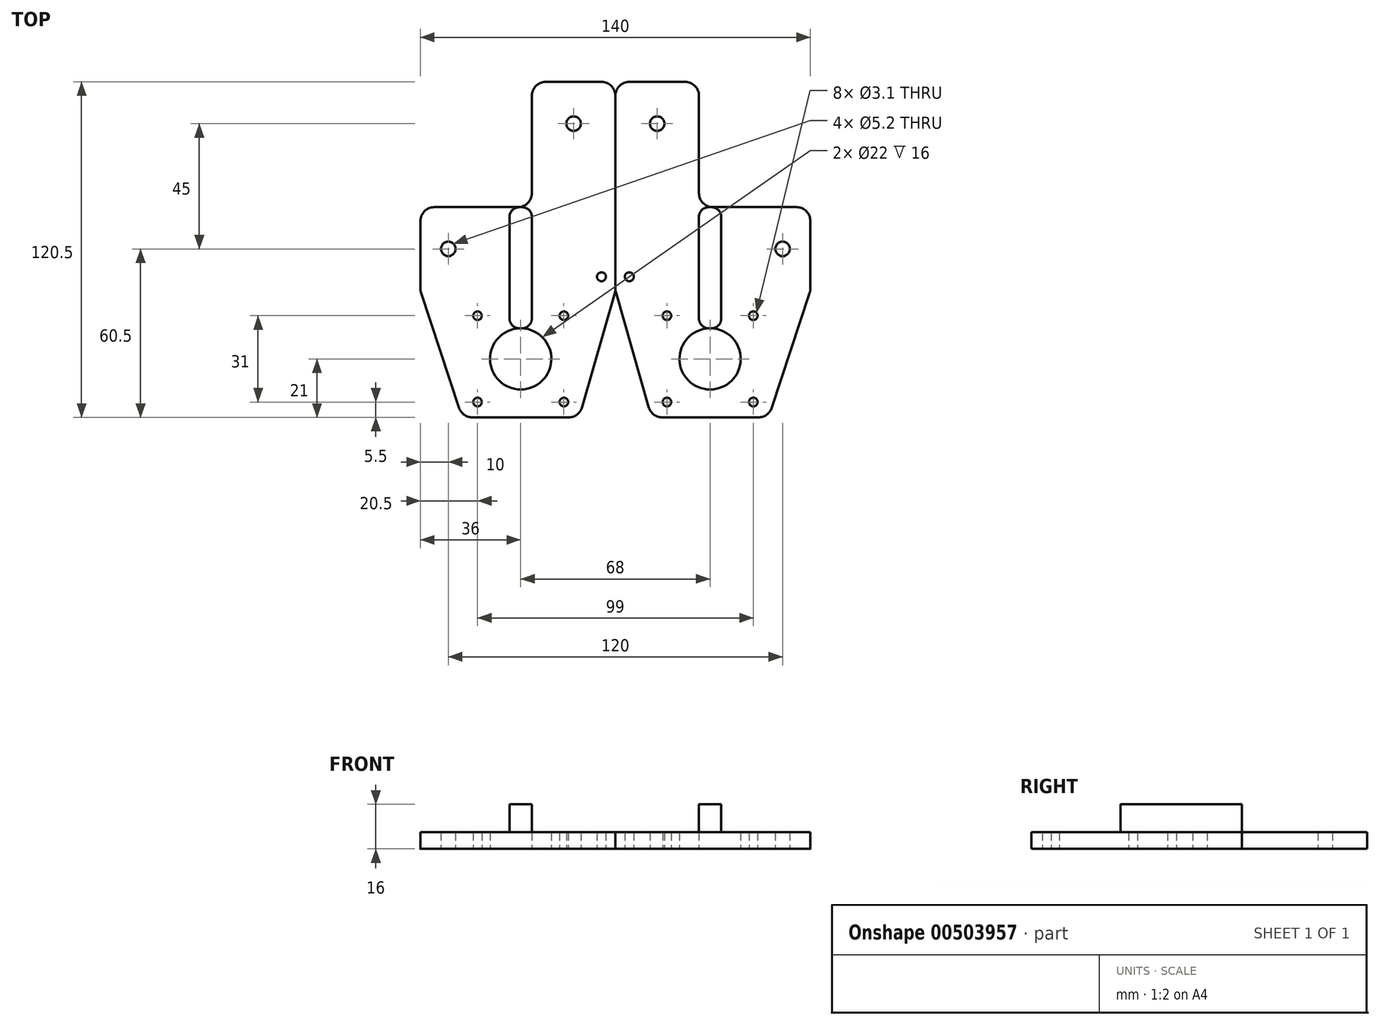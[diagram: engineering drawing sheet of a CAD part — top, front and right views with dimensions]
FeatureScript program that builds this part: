
annotation { "Feature Type Name" : "Feature", "Feature Type Description" : "" }
export const myFeature = defineFeature(function(context is Context, id is Id, definition is map)
    precondition{}
    {
        {
            var Q0;
            Q0=qCreatedBy(makeId("Top.planeOp"),FACE);
            var sketch = newSketch(context, id + "F0", { "sketchPlane" : qUnion([Q0])});
            skLineSegment(sketch, "E0.bottom", {"start": v(35, -60.25) * mm, "end": v(-35, -60.25) * mm});
            skLineSegment(sketch, "E0.left", {"start": v(35, -60.25) * mm, "end": v(35, 60.25) * mm});
            skLineSegment(sketch, "E0.right", {"start": v(-35, -60.25) * mm, "end": v(-35, 60.25) * mm});
            skPoint(sketch, "E0.middle", {"position": v(0, 0) * mm});
            skCircle(sketch, "E1", {"center": v(-1, -39.25) * mm, "radius": 11 * mm});
            skLineSegment(sketch, "E2.bottom", {"start": v(14.5, -54.75) * mm, "end": v(-16.5, -54.75) * mm, "construction": true});
            skLineSegment(sketch, "E2.top", {"start": v(14.5, -23.75) * mm, "end": v(-16.5, -23.75) * mm, "construction": true});
            skLineSegment(sketch, "E2.left", {"start": v(14.5, -54.75) * mm, "end": v(14.5, -23.75) * mm, "construction": true});
            skLineSegment(sketch, "E2.right", {"start": v(-16.5, -54.75) * mm, "end": v(-16.5, -23.75) * mm, "construction": true});
            skCircle(sketch, "E3", {"center": v(-16.5, -23.75) * mm, "radius": 1.55 * mm});
            skCircle(sketch, "E4", {"center": v(-16.5, -54.75) * mm, "radius": 1.55 * mm});
            skCircle(sketch, "E5", {"center": v(14.5, -54.75) * mm, "radius": 1.55 * mm});
            skCircle(sketch, "E6", {"center": v(14.5, -23.75) * mm, "radius": 1.55 * mm});
            skLineSegment(sketch, "E7", {"start": v(-35, 60.25) * mm, "end": v(35, 60.25) * mm});
            skLineSegment(sketch, "E8.bottom", {"start": v(35, 60.25) * mm, "end": v(-5, 60.25) * mm});
            skLineSegment(sketch, "E8.top", {"start": v(35, 15.25) * mm, "end": v(-5, 15.25) * mm});
            skLineSegment(sketch, "E8.left", {"start": v(35, 60.25) * mm, "end": v(35, 15.25) * mm});
            skLineSegment(sketch, "E8.right", {"start": v(-5, 60.25) * mm, "end": v(-5, 15.25) * mm});
            skLineSegment(sketch, "E9", {"start": v(-35, -14.75) * mm, "end": v(-22, -60.25) * mm});
            skLineSegment(sketch, "E10", {"start": v(35, -14.75) * mm, "end": v(20, -60.25) * mm});
            skLineSegment(sketch, "E11", {"start": v(-20, 60.25) * mm, "end": v(-20, 0.25) * mm, "construction": true});
            skCircle(sketch, "E12", {"center": v(-20, 45.25) * mm, "radius": 2.6 * mm});
            skLineSegment(sketch, "E13", {"start": v(35, 0.25) * mm, "end": v(-20, 0.25) * mm, "construction": true});
            skCircle(sketch, "E14", {"center": v(25, 0.25) * mm, "radius": 2.6 * mm});
            skCircle(sketch, "E15", {"center": v(-30, -9.75) * mm, "radius": 1.6 * mm});
            skSolve(sketch);
        }
        {
            var Q0;
            Q0=makeQuery(id+"F0.imprint","IMPRINT",FACE,{"disambiguationData":[TD([[makeQuery(id+"F0.imprint","IMPRINT",EDGE,{"derivedFrom":sQuery(id+"F0.wireOp",EDGE,"E1")}),-1.0]])]});
            extrude(context, id + "F1", {"entities" : qUnion([Q0]), "depth" : 6 * mm, "offsetDistance" : 25 * mm});
        }
        {
            var Q0;
            Q0=makeQuery(id+"F1.opExtrude","CAP_FACE",FACE,{"disambiguationData":[OSD([sQuery(id+"F0.wireOp",EDGE,"E0.bottom"),sQuery(id+"F0.wireOp",EDGE,"E0.left"),sQuery(id+"F0.wireOp",EDGE,"E0.right"),sQuery(id+"F0.wireOp",EDGE,"E1"),sQuery(id+"F0.wireOp",EDGE,"E3"),sQuery(id+"F0.wireOp",EDGE,"E4"),sQuery(id+"F0.wireOp",EDGE,"E5"),sQuery(id+"F0.wireOp",EDGE,"E6"),sQuery(id+"F0.wireOp",EDGE,"E7"),sQuery(id+"F0.wireOp",EDGE,"E8.top"),sQuery(id+"F0.wireOp",EDGE,"E8.right"),sQuery(id+"F0.wireOp",EDGE,"E9"),sQuery(id+"F0.wireOp",EDGE,"E10"),sQuery(id+"F0.wireOp",EDGE,"E12"),sQuery(id+"F0.wireOp",EDGE,"vjLGZ6ns-HpRk-grtY-ecPl-yhcPDgN8CZEY"),sQuery(id+"F0.wireOp",EDGE,"E14"),sQuery(id+"F0.wireOp",EDGE,"XwPzbW8u-APGH-DcEV-05JD-FyGxz5SDdVOS")])],"isStart":false});
            var sketch = newSketch(context, id + "F2", { "sketchPlane" : qUnion([Q0])});
            skLineSegment(sketch, "E16.bottom", {"start": v(3, -29) * mm, "end": v(-5, -29) * mm});
            skLineSegment(sketch, "E16.top", {"start": v(3, 15.25) * mm, "end": v(-5, 15.25) * mm});
            skLineSegment(sketch, "E16.left", {"start": v(3, -29) * mm, "end": v(3, 15.25) * mm});
            skLineSegment(sketch, "E16.right", {"start": v(-5, -29) * mm, "end": v(-5, 15.25) * mm});
            skPoint(sketch, "E16.middle", {"position": v(-1, -6.88) * mm});
            skSolve(sketch);
        }
        {
            var Q0;
            Q0=makeQuery(id+"F2.imprint","IMPRINT",FACE,{"disambiguationData":[TD([[makeQuery(id+"F2.imprint","IMPRINT",EDGE,{"derivedFrom":sQuery(id+"F2.wireOp",EDGE,"E16.top")}),1.0]])]});
            extrude(context, id + "F3", {"entities" : qUnion([Q0]), "operationType" : NewBodyOperationType.ADD, "depth" : 10 * mm, "offsetDistance" : 25 * mm});
        }
        {
            var Q0;
            Q0=makeQuery(id+"F1.opExtrude","SWEPT_EDGE",EDGE,{"disambiguationData":[OSD([sQuery(id+"F0.wireOp",EDGE,"E0.right"),sQuery(id+"F0.wireOp",EDGE,"E7")])]});
            var Q1;
            Q1=makeQuery(id+"F1.opExtrude","SWEPT_EDGE",EDGE,{"disambiguationData":[OSD([sQuery(id+"F0.wireOp",EDGE,"E7"),sQuery(id+"F0.wireOp",EDGE,"E8.bottom"),sQuery(id+"F0.wireOp",EDGE,"E8.right")])]});
            var Q2;
            Q2=makeQuery(id+"F1.opExtrude","SWEPT_EDGE",EDGE,{"disambiguationData":[OSD([sQuery(id+"F0.wireOp",EDGE,"E0.left"),sQuery(id+"F0.wireOp",EDGE,"E8.top"),sQuery(id+"F0.wireOp",EDGE,"E8.left")])]});
            var Q3;
            Q3=makeQuery(id+"F1.opExtrude","SWEPT_EDGE",EDGE,{"disambiguationData":[OSD([sQuery(id+"F0.wireOp",EDGE,"E8.top"),sQuery(id+"F0.wireOp",EDGE,"E8.right")])]});
            var Q4;
            Q4=makeQuery(id+"F1.opExtrude","SWEPT_EDGE",EDGE,{"disambiguationData":[OSD([sQuery(id+"F0.wireOp",EDGE,"E0.bottom"),sQuery(id+"F0.wireOp",EDGE,"E10")])]});
            var Q5;
            Q5=makeQuery(id+"F1.opExtrude","SWEPT_EDGE",EDGE,{"disambiguationData":[OSD([sQuery(id+"F0.wireOp",EDGE,"E0.bottom"),sQuery(id+"F0.wireOp",EDGE,"E9")])]});
            var Q6;
            Q6=makeQuery(id+"F1.opExtrude","SWEPT_EDGE",EDGE,{"disambiguationData":[OSD([sQuery(id+"F0.wireOp",EDGE,"E0.left"),sQuery(id+"F0.wireOp",EDGE,"E10")])]});
            var Q7;
            Q7=makeQuery(id+"F1.opExtrude","SWEPT_EDGE",EDGE,{"disambiguationData":[OSD([sQuery(id+"F0.wireOp",EDGE,"E0.right"),sQuery(id+"F0.wireOp",EDGE,"E9")])]});
            fillet(context, id + "F4", {"entities" : qUnion([Q0, Q1, Q2, Q3, Q4, Q5, Q6, Q7]), "radius" : 5 * mm, "tangentPropagation" : true, "allowEdgeOverflow" : false});
        }
        {
            var Q0;
            Q0=makeQuery(id+"F3.opExtrude","SWEPT_EDGE",EDGE,{"disambiguationData":[OSD([sQuery(id+"F0.wireOp",EDGE,"E8.right"),sQuery(id+"F2.wireOp",EDGE,"E16.top"),sQuery(id+"F2.wireOp",EDGE,"E16.right")])]});
            var Q1;
            Q1=makeQuery(id+"F3.opExtrude","SWEPT_EDGE",EDGE,{"disambiguationData":[OSD([sQuery(id+"F0.wireOp",EDGE,"E8.top"),sQuery(id+"F2.wireOp",EDGE,"E16.top"),sQuery(id+"F2.wireOp",EDGE,"E16.left")])]});
            var Q2;
            Q2=makeQuery(id+"F3.opExtrude","SWEPT_EDGE",EDGE,{"disambiguationData":[OSD([sQuery(id+"F0.wireOp",EDGE,"E1"),sQuery(id+"F2.wireOp",EDGE,"E16.bottom"),sQuery(id+"F2.wireOp",EDGE,"E16.right")])]});
            var Q3;
            Q3=makeQuery(id+"F3.opExtrude","SWEPT_EDGE",EDGE,{"disambiguationData":[OSD([sQuery(id+"F0.wireOp",EDGE,"E1"),sQuery(id+"F2.wireOp",EDGE,"E16.bottom"),sQuery(id+"F2.wireOp",EDGE,"E16.left")])]});
            fillet(context, id + "F5", {"entities" : qUnion([Q0, Q1, Q2, Q3]), "radius" : 3.5 * mm, "tangentPropagation" : true, "allowEdgeOverflow" : false});
        }
        {
            var Q0;
            Q0=makeQuery(id+"F1.opExtrude","SWEPT_BODY",BODY,{"disambiguationData":[OSD([sQuery(id+"F0.wireOp",EDGE,"E0.bottom"),sQuery(id+"F0.wireOp",EDGE,"E0.left"),sQuery(id+"F0.wireOp",EDGE,"E0.right"),sQuery(id+"F0.wireOp",EDGE,"E1"),sQuery(id+"F0.wireOp",EDGE,"E3"),sQuery(id+"F0.wireOp",EDGE,"E4"),sQuery(id+"F0.wireOp",EDGE,"E5"),sQuery(id+"F0.wireOp",EDGE,"E6"),sQuery(id+"F0.wireOp",EDGE,"E7"),sQuery(id+"F0.wireOp",EDGE,"E8.top"),sQuery(id+"F0.wireOp",EDGE,"E8.right"),sQuery(id+"F0.wireOp",EDGE,"E9"),sQuery(id+"F0.wireOp",EDGE,"E10"),sQuery(id+"F0.wireOp",EDGE,"E12"),sQuery(id+"F0.wireOp",EDGE,"vjLGZ6ns-HpRk-grtY-ecPl-yhcPDgN8CZEY"),sQuery(id+"F0.wireOp",EDGE,"E14"),sQuery(id+"F0.wireOp",EDGE,"XwPzbW8u-APGH-DcEV-05JD-FyGxz5SDdVOS")])]});
            var Q1;
            Q1=makeQuery(id+"F1.opExtrude","SWEPT_FACE",FACE,{"disambiguationData":[OSD([sQuery(id+"F0.wireOp",EDGE,"E0.right")])]});
            mirror(context, id + "F6", {"entities" : qUnion([Q0]), "mirrorPlane" : qUnion([Q1])});
        }
    });
